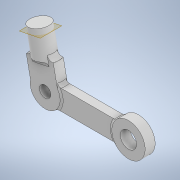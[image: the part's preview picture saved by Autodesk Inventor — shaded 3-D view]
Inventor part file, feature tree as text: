
AUTODESK INVENTOR PART (.ipt)
format: ipt  version: 2022.6 (Build 266554000, 554)  size: 261,632 bytes
history: native  units: mm
features: sketch x7, extrude x6, fillet x3, projected_geometry x2, revolve x1, plane x1
ambient origin geometry x8: Origin, YZ Plane, XZ Plane, XY Plane, X Axis, Y Axis, Z Axis, Center Point
bodies: Solid1 (feature_tree)
feature tree (20):
  extrude  "Extrusion1"  Depth=3.0mm TaperAngle=0.0deg
  extrude  "Extrusion2"  Depth=3.0mm
  revolve  "Revolution1"  [1 undecoded]
  extrude  "Extrusion3"  Depth=8.0mm
  extrude  "Extrusion4"  Depth=17.715092mm
  extrude  "Extrusion5"  TaperAngle=90.0deg  [1 undecoded]
  fillet  "Fillet1"  [1 undecoded]
  fillet  "Fillet2"  Radius=3.0mm
  plane  "Work Plane1"
  extrude  "Extrusion6"  Depth=10.0mm TaperAngle=0.0deg
  fillet  "Fillet3"  Radius=4.9mm
  sketch  "Sketch1"  dims[d2=25.0mm d3=3.0mm d4=0.0mm]
  sketch  "Sketch2"  dims[d5=2.0mm d7=3.0mm]
  projected_geometry  "Projected Loop1"
  sketch  "Sketch3"  dims[d8=2.5mm d9=0.0mm d13=8.0mm]
  sketch  "Sketch4"  dims[d14=1.5mm d15=8.0mm]
  projected_geometry  "Projected Loop2"
  sketch  "Sketch5"  dims[d16=3.0mm d17=17.715092mm]
  sketch  "Sketch6"  dims[d18=6.834775mm d19=90.0deg d21=0.0mm d22=0.0mm d23=3.0mm]
  sketch  "Sketch7"  dims[d24=2.828mm d25=10.0mm d26=0.0mm d27=4.9mm d28=10.0mm d30=5.687mm d31=5.9mm d32=6.0mm d33=0.0mm d34=1.4mm d35=3.4mm d36=9.0mm d37=1.0mm d38=-1.5mm d39=6.1mm d40=1.0mm d41=0.0mm d42=0.5mm d20=0.872665mm d29=0.5mm]
note: 3 required parameter values undecoded (feature->parameter linkage not recoverable at this tier; creation-order binding heuristic only, values carry confidence <= 0.55)